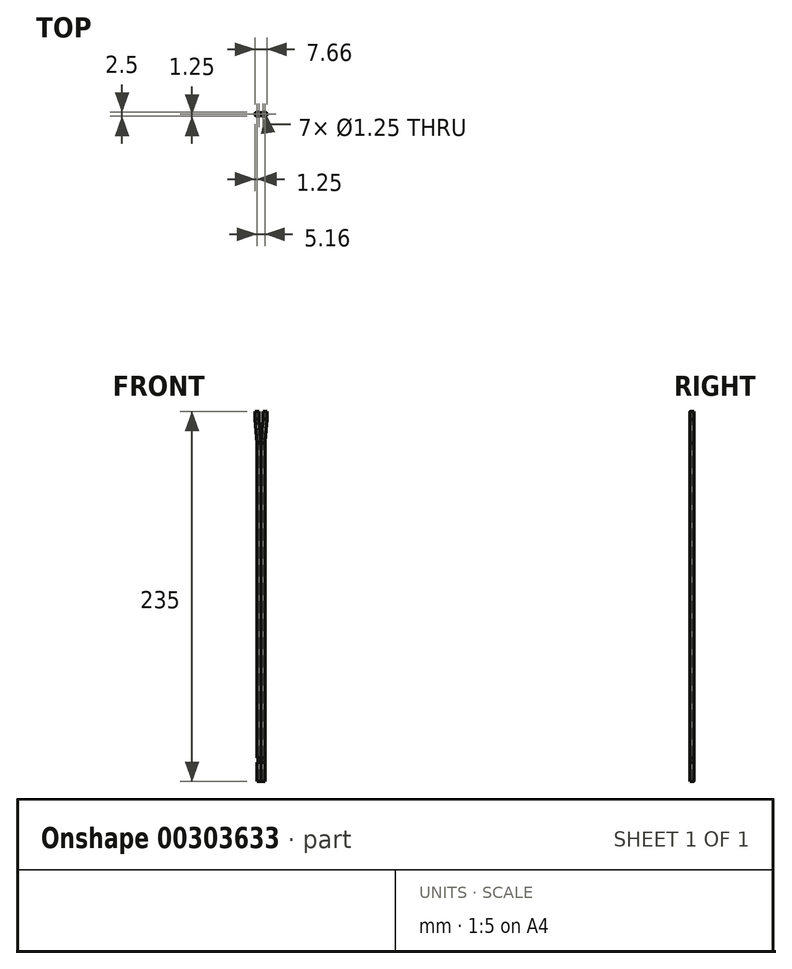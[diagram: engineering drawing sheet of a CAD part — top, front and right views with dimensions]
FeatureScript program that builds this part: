
annotation { "Feature Type Name" : "Feature", "Feature Type Description" : "" }
export const myFeature = defineFeature(function(context is Context, id is Id, definition is map)
    precondition{}
    {
        {
            var Q0;
            Q0=qCreatedBy(makeId("Front.planeOp"),FACE);
            var sketch = newSketch(context, id + "F0", { "sketchPlane" : qUnion([Q0])});
            skLineSegment(sketch, "E0", {"start": v(-1.25, 0) * mm, "end": v(-1.25, 200) * mm});
            skLineSegment(sketch, "E1", {"start": v(-1.25, 200) * mm, "end": v(-2.58, 215) * mm});
            skLineSegment(sketch, "E2", {"start": v(-2.58, 215) * mm, "end": v(-2.58, 220) * mm});
            skLineSegment(sketch, "E3.MirrorCS", {"start": v(1.25, 200) * mm, "end": v(2.58, 215) * mm});
            skLineSegment(sketch, "E4.MirrorCS", {"start": v(2.58, 215) * mm, "end": v(2.58, 220) * mm});
            skLineSegment(sketch, "E5.MirrorCS", {"start": v(1.25, 0) * mm, "end": v(1.25, 200) * mm});
            skSolve(sketch);
        }
        {
            var Q0;
            Q0=qCreatedBy(makeId("Top.planeOp"),FACE);
            var sketch = newSketch(context, id + "F1", { "sketchPlane" : qUnion([Q0])});
            skCircle(sketch, "E6", {"center": v(-1.25, 0) * mm, "radius": 0.62 * mm});
            skCircle(sketch, "E7.MirrorC", {"center": v(1.25, 0) * mm, "radius": 0.62 * mm});
            skCircle(sketch, "E8", {"center": v(-1.25, 0) * mm, "radius": 1.25 * mm});
            skCircle(sketch, "E9.MirrorC", {"center": v(1.25, 0) * mm, "radius": 1.25 * mm});
            skSolve(sketch);
        }
        {
            var Q0;
            Q0=makeQuery(id+"F1.imprint","IMPRINT",FACE,{"disambiguationData":[TD([[makeQuery(id+"F1.imprint","IMPRINT",EDGE,{"derivedFrom":sQuery(id+"F1.wireOp",EDGE,"E7.MirrorC")}),-1.0]])]});
            var Q1;
            Q1=sQuery(id+"F0.wireOp",EDGE,"E5.MirrorCS");
            var Q2;
            Q2=sQuery(id+"F0.wireOp",EDGE,"E3.MirrorCS");
            var Q3;
            Q3=sQuery(id+"F0.wireOp",EDGE,"E4.MirrorCS");
            sweep(context, id + "F2", {"profiles" : qUnion([Q0]), "path" : qUnion([Q1, Q2, Q3])});
        }
        {
            var Q0;
            Q0=makeQuery(id+"F1.imprint","IMPRINT",FACE,{"disambiguationData":[TD([[makeQuery(id+"F1.imprint","IMPRINT",EDGE,{"derivedFrom":sQuery(id+"F1.wireOp",EDGE,"E6")}),1.0]])]});
            var Q1;
            Q1=sQuery(id+"F0.wireOp",EDGE,"E0");
            var Q2;
            Q2=sQuery(id+"F0.wireOp",EDGE,"E1");
            var Q3;
            Q3=sQuery(id+"F0.wireOp",EDGE,"E2");
            sweep(context, id + "F3", {"profiles" : qUnion([Q0]), "path" : qUnion([Q1, Q2, Q3])});
        }
        {
            var Q0;
            Q0=makeQuery(id+"F1.imprint","IMPRINT",FACE,{"disambiguationData":[TD([[makeQuery(id+"F1.imprint","IMPRINT",EDGE,{"derivedFrom":sQuery(id+"F1.wireOp",EDGE,"E7.MirrorC")}),1.0]])]});
            var Q1;
            Q1=sQuery(id+"F0.wireOp",EDGE,"E3.MirrorCS");
            var Q2;
            Q2=sQuery(id+"F0.wireOp",EDGE,"E4.MirrorCS");
            var Q3;
            Q3=sQuery(id+"F0.wireOp",EDGE,"E5.MirrorCS");
            sweep(context, id + "F4", {"profiles" : qUnion([Q0]), "path" : qUnion([Q1, Q2, Q3])});
        }
        {
            var Q0;
            Q0=makeQuery(id+"F1.imprint","IMPRINT",FACE,{"disambiguationData":[TD([[makeQuery(id+"F1.imprint","IMPRINT",EDGE,{"derivedFrom":sQuery(id+"F1.wireOp",EDGE,"E6")}),-1.0]])]});
            var Q1;
            Q1=sQuery(id+"F0.wireOp",EDGE,"E0");
            var Q2;
            Q2=sQuery(id+"F0.wireOp",EDGE,"E1");
            var Q3;
            Q3=sQuery(id+"F0.wireOp",EDGE,"E2");
            sweep(context, id + "F5", {"profiles" : qUnion([Q0]), "path" : qUnion([Q1, Q2, Q3])});
        }
        {
            var Q0;
            Q0=makeQuery(id+"F1.imprint","IMPRINT",FACE,{"disambiguationData":[TD([[makeQuery(id+"F1.imprint","IMPRINT",EDGE,{"derivedFrom":sQuery(id+"F1.wireOp",EDGE,"E6")}),1.0]])]});
            var Q1;
            Q1=makeQuery(id+"F1.imprint","IMPRINT",FACE,{"disambiguationData":[TD([[makeQuery(id+"F1.imprint","IMPRINT",EDGE,{"derivedFrom":sQuery(id+"F1.wireOp",EDGE,"E7.MirrorC")}),-1.0]])]});
            extrude(context, id + "F6", {"entities" : qUnion([Q0, Q1]), "oppositeDirection" : true, "depth" : 15 * mm});
        }
        {
            var Q0;
            Q0 = qSketchRegion(id + "F1", true);
            extrude(context, id + "F7", {"entities" : qUnion([Q0]), "oppositeDirection" : true, "depth" : 15 * mm, "hasSecondDirection" : true, "secondDirectionOppositeDirection" : true, "secondDirectionDepth" : 3 * mm});
        }
    });
